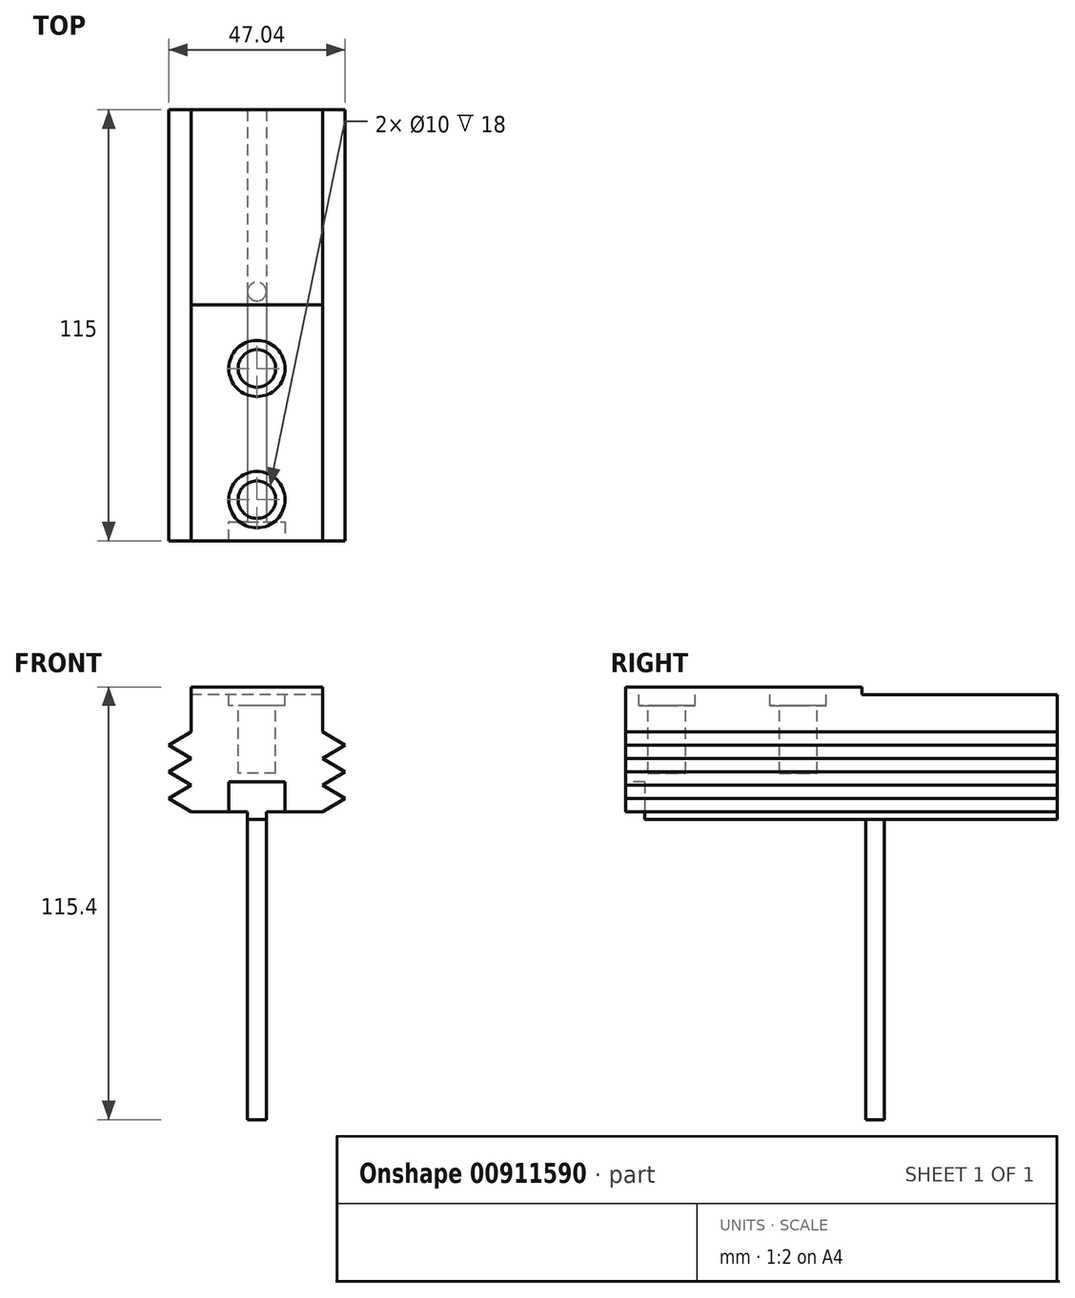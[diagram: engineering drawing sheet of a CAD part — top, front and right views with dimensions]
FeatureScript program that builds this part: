
annotation { "Feature Type Name" : "Feature", "Feature Type Description" : "" }
export const myFeature = defineFeature(function(context is Context, id is Id, definition is map)
    precondition{}
    {
        {
            var Q0;
            Q0=qCreatedBy(makeId("Top.planeOp"),FACE);
            var sketch = newSketch(context, id + "F0", { "sketchPlane" : qUnion([Q0])});
            skLineSegment(sketch, "E0.bottom", {"start": v(-17.99, 0) * mm, "end": v(17.01, 0) * mm});
            skLineSegment(sketch, "E0.top", {"start": v(-17.99, -63) * mm, "end": v(17.01, -63) * mm});
            skLineSegment(sketch, "E0.left", {"start": v(-17.99, 0) * mm, "end": v(-17.99, -63) * mm});
            skLineSegment(sketch, "E0.right", {"start": v(17.01, 0) * mm, "end": v(17.01, -63) * mm});
            skSolve(sketch);
        }
        {
            var Q0;
            Q0=makeQuery(id+"F0.imprint","IMPRINT",FACE,{"disambiguationData":[TD([[makeQuery(id+"F0.imprint","IMPRINT",EDGE,{"derivedFrom":sQuery(id+"F0.wireOp",EDGE,"E0.bottom")}),-1.0]])]});
            extrude(context, id + "F1", {"entities" : qUnion([Q0]), "oppositeDirection" : true, "depth" : 35.3 * mm, "offsetDistance" : 25 * mm});
        }
        {
            var Q0;
            Q0=makeQuery(id+"F1.opExtrude","SWEPT_FACE",FACE,{"disambiguationData":[OSD([sQuery(id+"F0.wireOp",EDGE,"E0.top")])]});
            var sketch = newSketch(context, id + "F2", { "sketchPlane" : qUnion([Q0])});
            skLineSegment(sketch, "E1", {"start": v(-17.99, -12) * mm, "end": v(-24, -15.55) * mm});
            skLineSegment(sketch, "E2", {"start": v(-24, -15.55) * mm, "end": v(-17.99, -19.1) * mm});
            skLineSegment(sketch, "E3", {"start": v(-17.99, -19.1) * mm, "end": v(-24, -22.65) * mm});
            skLineSegment(sketch, "E4", {"start": v(-24, -22.65) * mm, "end": v(-17.99, -26.2) * mm});
            skLineSegment(sketch, "E5", {"start": v(-17.99, -26.2) * mm, "end": v(-24, -29.75) * mm});
            skLineSegment(sketch, "E6", {"start": v(-24, -29.75) * mm, "end": v(-17.99, -33.3) * mm});
            skLineSegment(sketch, "E7", {"start": v(17.01, -33.3) * mm, "end": v(23.03, -29.75) * mm});
            skLineSegment(sketch, "E8", {"start": v(23.03, -29.75) * mm, "end": v(17.01, -26.2) * mm});
            skLineSegment(sketch, "E9", {"start": v(17.01, -26.2) * mm, "end": v(23.03, -22.65) * mm});
            skLineSegment(sketch, "E10", {"start": v(23.03, -22.65) * mm, "end": v(17.01, -19.1) * mm});
            skLineSegment(sketch, "E11", {"start": v(17.01, -19.1) * mm, "end": v(23.03, -15.55) * mm});
            skLineSegment(sketch, "E12", {"start": v(23.03, -15.55) * mm, "end": v(17.01, -12) * mm});
            skLineSegment(sketch, "E13", {"start": v(-17.99, -33.3) * mm, "end": v(-2.99, -33.3) * mm});
            skLineSegment(sketch, "E14", {"start": v(17.01, -33.3) * mm, "end": v(2.01, -33.3) * mm});
            skLineSegment(sketch, "E15", {"start": v(-2.99, -33.3) * mm, "end": v(-2.99, -35.3) * mm});
            skLineSegment(sketch, "E16", {"start": v(2.01, -33.3) * mm, "end": v(2.01, -35.3) * mm});
            skLineSegment(sketch, "E17", {"start": v(2.01, -35.3) * mm, "end": v(-2.99, -35.3) * mm});
            skLineSegment(sketch, "E18", {"start": v(-17.99, 0) * mm, "end": v(-17.99, -12) * mm});
            skLineSegment(sketch, "E19", {"start": v(17.01, 0) * mm, "end": v(17.01, -12) * mm});
            skSolve(sketch);
        }
        {
            var Q0;
            Q0=qSketchRegion(id+"F2",true);
            var Q1;
            {var subQ0=sQuery(id+"F2.wireOp",EDGE,"E14");Q1=makeQuery(id+"F2.imprint","IMPRINT",FACE,{"disambiguationData":[TD([[makeQuery(id+"F2.imprint","IMPRINT",EDGE,{"derivedFrom":subQ0}),1.0]])]});}
            var Q2;
            {var subQ0=sQuery(id+"F2.wireOp",EDGE,"E13");Q2=makeQuery(id+"F2.imprint","IMPRINT",FACE,{"disambiguationData":[TD([[makeQuery(id+"F2.imprint","IMPRINT",EDGE,{"derivedFrom":subQ0}),-1.0]])]});}
            extrude(context, id + "F3", {"entities" : qUnion([Q0, Q1, Q2]), "operationType" : NewBodyOperationType.REMOVE, "endBound" : BoundingType.THROUGH_ALL, "oppositeDirection" : true, "depth" : 25 * mm, "offsetDistance" : 25 * mm});
        }
        {
            var Q0;
            {var subQ0=sQuery(id+"F2.wireOp",EDGE,"E1");Q0=makeQuery(id+"F2.imprint","IMPRINT",FACE,{"disambiguationData":[TD([[makeQuery(id+"F2.imprint","IMPRINT",EDGE,{"derivedFrom":subQ0}),1.0]])]});}
            var Q1;
            {var subQ0=sQuery(id+"F2.wireOp",EDGE,"E3");Q1=makeQuery(id+"F2.imprint","IMPRINT",FACE,{"disambiguationData":[TD([[makeQuery(id+"F2.imprint","IMPRINT",EDGE,{"derivedFrom":subQ0}),1.0]])]});}
            var Q2;
            {var subQ0=sQuery(id+"F2.wireOp",EDGE,"E5");Q2=makeQuery(id+"F2.imprint","IMPRINT",FACE,{"disambiguationData":[TD([[makeQuery(id+"F2.imprint","IMPRINT",EDGE,{"derivedFrom":subQ0}),1.0]])]});}
            var Q3;
            {var subQ0=sQuery(id+"F2.wireOp",EDGE,"E7");Q3=makeQuery(id+"F2.imprint","IMPRINT",FACE,{"disambiguationData":[TD([[makeQuery(id+"F2.imprint","IMPRINT",EDGE,{"derivedFrom":subQ0}),1.0]])]});}
            var Q4;
            {var subQ0=sQuery(id+"F2.wireOp",EDGE,"E11");Q4=makeQuery(id+"F2.imprint","IMPRINT",FACE,{"disambiguationData":[TD([[makeQuery(id+"F2.imprint","IMPRINT",EDGE,{"derivedFrom":subQ0}),1.0]])]});}
            var Q5;
            {var subQ0=sQuery(id+"F2.wireOp",EDGE,"E9");Q5=makeQuery(id+"F2.imprint","IMPRINT",FACE,{"disambiguationData":[TD([[makeQuery(id+"F2.imprint","IMPRINT",EDGE,{"derivedFrom":subQ0}),1.0]])]});}
            extrude(context, id + "F4", {"entities" : qUnion([Q0, Q1, Q2, Q3, Q4, Q5]), "operationType" : NewBodyOperationType.ADD, "oppositeDirection" : true, "depth" : 63 * mm, "offsetDistance" : 25 * mm});
        }
        {
            var Q0;
            Q0=makeQuery(id+"F1.opExtrude","CAP_FACE",FACE,{"disambiguationData":[OSD([sQuery(id+"F0.wireOp",EDGE,"E0.bottom"),sQuery(id+"F0.wireOp",EDGE,"E0.top"),sQuery(id+"F0.wireOp",EDGE,"E0.left"),sQuery(id+"F0.wireOp",EDGE,"E0.right")])],"isStart":true});
            var sketch = newSketch(context, id + "F5", { "sketchPlane" : qUnion([Q0])});
            skCircle(sketch, "E20", {"center": v(-0.49, -52) * mm, "radius": 5 * mm});
            skCircle(sketch, "E21", {"center": v(-0.49, -17) * mm, "radius": 5 * mm});
            skCircle(sketch, "E22", {"center": v(-0.49, -17) * mm, "radius": 7.5 * mm});
            skCircle(sketch, "E23", {"center": v(-0.49, -52) * mm, "radius": 7.5 * mm});
            skSolve(sketch);
        }
        {
            var Q0;
            Q0=makeQuery(id+"F5.imprint","IMPRINT",FACE,{"disambiguationData":[TD([[makeQuery(id+"F5.imprint","IMPRINT",EDGE,{"derivedFrom":sQuery(id+"F5.wireOp",EDGE,"E21")}),1.0]])]});
            var Q1;
            Q1=makeQuery(id+"F5.imprint","IMPRINT",FACE,{"disambiguationData":[TD([[makeQuery(id+"F5.imprint","IMPRINT",EDGE,{"derivedFrom":sQuery(id+"F5.wireOp",EDGE,"E20")}),1.0]])]});
            extrude(context, id + "F6", {"entities" : qUnion([Q0, Q1]), "operationType" : NewBodyOperationType.REMOVE, "oppositeDirection" : true, "depth" : 23 * mm, "offsetDistance" : 25 * mm});
        }
        {
            var Q0;
            Q0=qSketchRegion(id+"F5",true);
            extrude(context, id + "F7", {"entities" : qUnion([Q0]), "operationType" : NewBodyOperationType.REMOVE, "oppositeDirection" : true, "depth" : 5 * mm, "offsetDistance" : 25 * mm});
        }
        {
            var Q0;
            {var subQ0=sQuery(id+"F0.wireOp",EDGE,"E0.right");var subQ1=sQuery(id+"F0.wireOp",EDGE,"E0.top");var subQ2=sQuery(id+"F0.wireOp",EDGE,"E0.left");Q0=makeQuery(id+"F4.boolean.opBoolean","MERGE",FACE,{"derivedFrom":[makeQuery(id+"F1.opExtrude","SWEPT_FACE",FACE,{"disambiguationData":[OSD([subQ1])]}),makeQuery(id+"F4.opExtrude","CAP_FACE",FACE,{"disambiguationData":[OSD([subQ1,subQ2,sQuery(id+"F2.wireOp",EDGE,"E1"),sQuery(id+"F2.wireOp",EDGE,"E2")])],"isStart":true}),makeQuery(id+"F4.opExtrude","CAP_FACE",FACE,{"disambiguationData":[OSD([subQ1,subQ2,sQuery(id+"F2.wireOp",EDGE,"E3"),sQuery(id+"F2.wireOp",EDGE,"E4")])],"isStart":true}),makeQuery(id+"F4.opExtrude","CAP_FACE",FACE,{"disambiguationData":[OSD([subQ1,subQ2,sQuery(id+"F2.wireOp",EDGE,"E5"),sQuery(id+"F2.wireOp",EDGE,"E6")])],"isStart":true}),makeQuery(id+"F4.opExtrude","CAP_FACE",FACE,{"disambiguationData":[OSD([subQ1,subQ0,sQuery(id+"F2.wireOp",EDGE,"E7"),sQuery(id+"F2.wireOp",EDGE,"E8")])],"isStart":true}),makeQuery(id+"F4.opExtrude","CAP_FACE",FACE,{"disambiguationData":[OSD([subQ1,subQ0,sQuery(id+"F2.wireOp",EDGE,"E9"),sQuery(id+"F2.wireOp",EDGE,"E10")])],"isStart":true}),makeQuery(id+"F4.opExtrude","CAP_FACE",FACE,{"disambiguationData":[OSD([subQ1,subQ0,sQuery(id+"F2.wireOp",EDGE,"E11"),sQuery(id+"F2.wireOp",EDGE,"E12")])],"isStart":true})]});}
            var sketch = newSketch(context, id + "F8", { "sketchPlane" : qUnion([Q0])});
            skLineSegment(sketch, "E24", {"start": v(-0.49, -35.3) * mm, "end": v(-0.49, -22.62) * mm});
            skLineSegment(sketch, "E25.bottom", {"start": v(-7.99, -25.3) * mm, "end": v(7.01, -25.3) * mm});
            skLineSegment(sketch, "E25.top", {"start": v(-7.99, -35.5) * mm, "end": v(7.01, -35.5) * mm});
            skLineSegment(sketch, "E25.left", {"start": v(-7.99, -25.3) * mm, "end": v(-7.99, -35.5) * mm});
            skLineSegment(sketch, "E25.right", {"start": v(7.01, -25.3) * mm, "end": v(7.01, -35.5) * mm});
            skSolve(sketch);
        }
        {
            var Q0;
            Q0=qSketchRegion(id+"F8",true);
            extrude(context, id + "F9", {"entities" : qUnion([Q0]), "operationType" : NewBodyOperationType.REMOVE, "oppositeDirection" : true, "depth" : 5 * mm, "offsetDistance" : 25 * mm});
        }
        {
            var Q0;
            {var subQ0=sQuery(id+"F0.wireOp",EDGE,"E0.right");var subQ1=sQuery(id+"F0.wireOp",EDGE,"E0.top");var subQ2=sQuery(id+"F0.wireOp",EDGE,"E0.left");Q0=makeQuery(id+"F4.boolean.opBoolean","MERGE",FACE,{"derivedFrom":[makeQuery(id+"F1.opExtrude","SWEPT_FACE",FACE,{"disambiguationData":[OSD([sQuery(id+"F0.wireOp",EDGE,"E0.bottom")])]}),makeQuery(id+"F4.opExtrude","CAP_FACE",FACE,{"disambiguationData":[OSD([subQ1,subQ2,sQuery(id+"F2.wireOp",EDGE,"E1"),sQuery(id+"F2.wireOp",EDGE,"E2")])],"isStart":false}),makeQuery(id+"F4.opExtrude","CAP_FACE",FACE,{"disambiguationData":[OSD([subQ1,subQ2,sQuery(id+"F2.wireOp",EDGE,"E3"),sQuery(id+"F2.wireOp",EDGE,"E4")])],"isStart":false}),makeQuery(id+"F4.opExtrude","CAP_FACE",FACE,{"disambiguationData":[OSD([subQ1,subQ2,sQuery(id+"F2.wireOp",EDGE,"E5"),sQuery(id+"F2.wireOp",EDGE,"E6")])],"isStart":false}),makeQuery(id+"F4.opExtrude","CAP_FACE",FACE,{"disambiguationData":[OSD([subQ1,subQ0,sQuery(id+"F2.wireOp",EDGE,"E7"),sQuery(id+"F2.wireOp",EDGE,"E8")])],"isStart":false}),makeQuery(id+"F4.opExtrude","CAP_FACE",FACE,{"disambiguationData":[OSD([subQ1,subQ0,sQuery(id+"F2.wireOp",EDGE,"E9"),sQuery(id+"F2.wireOp",EDGE,"E10")])],"isStart":false}),makeQuery(id+"F4.opExtrude","CAP_FACE",FACE,{"disambiguationData":[OSD([subQ1,subQ0,sQuery(id+"F2.wireOp",EDGE,"E11"),sQuery(id+"F2.wireOp",EDGE,"E12")])],"isStart":false})]});}
            var sketch = newSketch(context, id + "F10", { "sketchPlane" : qUnion([Q0])});
            skLineSegment(sketch, "E26.bottom", {"start": v(-17.01, -2) * mm, "end": v(17.99, -2) * mm});
            skLineSegment(sketch, "E26.left", {"start": v(-17.01, -2) * mm, "end": v(-17.01, -12) * mm});
            skLineSegment(sketch, "E26.right", {"start": v(17.99, -2) * mm, "end": v(17.99, -12) * mm});
            skLineSegment(sketch, "E27", {"start": v(-17.01, -12) * mm, "end": v(-23.03, -15.55) * mm});
            skLineSegment(sketch, "E28", {"start": v(-23.03, -15.55) * mm, "end": v(-17.01, -19.1) * mm});
            skLineSegment(sketch, "E29", {"start": v(-17.01, -19.1) * mm, "end": v(-23.03, -22.65) * mm});
            skLineSegment(sketch, "E30", {"start": v(-23.03, -22.65) * mm, "end": v(-17.01, -26.2) * mm});
            skLineSegment(sketch, "E31", {"start": v(-17.01, -26.2) * mm, "end": v(-23.03, -29.75) * mm});
            skLineSegment(sketch, "E32", {"start": v(-23.03, -29.75) * mm, "end": v(-17.01, -33.3) * mm});
            skLineSegment(sketch, "E33", {"start": v(-17.01, -33.3) * mm, "end": v(-2.01, -33.3) * mm});
            skLineSegment(sketch, "E34", {"start": v(-2.01, -33.3) * mm, "end": v(-2.01, -35.3) * mm});
            skLineSegment(sketch, "E35", {"start": v(-2.01, -35.3) * mm, "end": v(2.99, -35.3) * mm});
            skLineSegment(sketch, "E36", {"start": v(2.99, -35.3) * mm, "end": v(2.99, -33.3) * mm});
            skLineSegment(sketch, "E37", {"start": v(2.99, -33.3) * mm, "end": v(17.99, -33.3) * mm});
            skLineSegment(sketch, "E38", {"start": v(17.99, -33.3) * mm, "end": v(24, -29.75) * mm});
            skLineSegment(sketch, "E39", {"start": v(24, -29.75) * mm, "end": v(17.99, -26.2) * mm});
            skLineSegment(sketch, "E40", {"start": v(17.99, -26.2) * mm, "end": v(24, -22.65) * mm});
            skLineSegment(sketch, "E41", {"start": v(24, -22.65) * mm, "end": v(17.99, -19.1) * mm});
            skLineSegment(sketch, "E42", {"start": v(17.99, -19.1) * mm, "end": v(24, -15.55) * mm});
            skLineSegment(sketch, "E43", {"start": v(24, -15.55) * mm, "end": v(17.99, -12) * mm});
            skSolve(sketch);
        }
        {
            var Q0;
            Q0=qSketchRegion(id+"F10",true);
            var Q1;
            Q1=makeQuery(id+"F10.imprint","IMPRINT",FACE,{"disambiguationData":[TD([[makeQuery(id+"F10.imprint","IMPRINT",EDGE,{"derivedFrom":sQuery(id+"F10.wireOp",EDGE,"E26.bottom")}),-1.0]])]});
            extrude(context, id + "F11", {"entities" : qUnion([Q0, Q1]), "operationType" : NewBodyOperationType.ADD, "depth" : 52 * mm, "offsetDistance" : 25 * mm});
        }
        {
            var Q0;
            Q0=makeQuery(id+"F11.boolean.opBoolean","MERGE",FACE,{"derivedFrom":[makeQuery(id+"F1.opExtrude","CAP_FACE",FACE,{"disambiguationData":[OSD([sQuery(id+"F0.wireOp",EDGE,"E0.bottom"),sQuery(id+"F0.wireOp",EDGE,"E0.top"),sQuery(id+"F0.wireOp",EDGE,"E0.left"),sQuery(id+"F0.wireOp",EDGE,"E0.right")])],"isStart":false}),makeQuery(id+"F11.opExtrude","SWEPT_FACE",FACE,{"disambiguationData":[OSD([sQuery(id+"F10.wireOp",EDGE,"E35")])]})]});
            var sketch = newSketch(context, id + "F12", { "sketchPlane" : qUnion([Q0])});
            skCircle(sketch, "E44", {"center": v(-0.49, -3.5) * mm, "radius": 2.5 * mm});
            skSolve(sketch);
        }
        {
            var Q0;
            Q0 = qSketchRegion(id + "F12", true);
            extrude(context, id + "F13", {"entities" : qUnion([Q0]), "operationType" : NewBodyOperationType.ADD, "depth" : 80.1 * mm, "offsetDistance" : 25 * mm});
        }
    });
